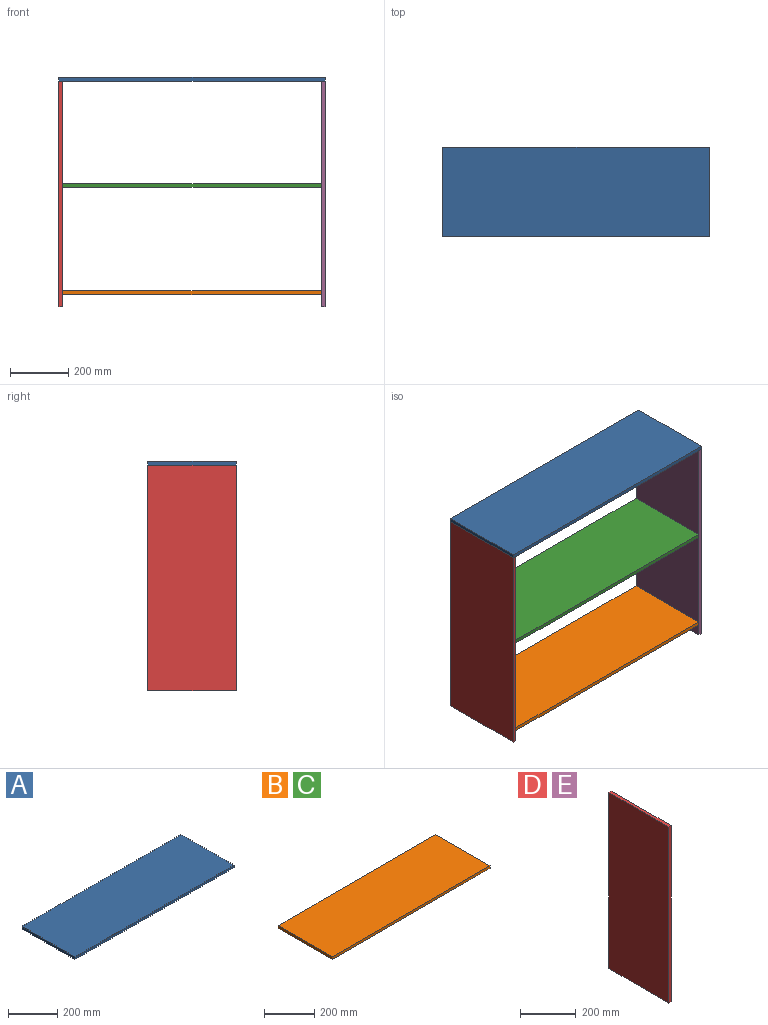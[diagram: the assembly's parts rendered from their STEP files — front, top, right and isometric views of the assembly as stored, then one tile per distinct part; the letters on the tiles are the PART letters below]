
ASSEMBLY  parts=5 mates=10
PART A: 6 faces, bbox 914.4x304.8x12.7 mm
  f0: plane 304.8x12.7mm, normal (-1,0,0), area 3871mm2, adj f1,f3,f4,f5
  f1: plane 914.4x304.8mm, normal (0,0,-1), area 278709.1mm2, adj f0,f2,f4,f5
  f2: plane 304.8x12.7mm, normal (1,0,0), area 3871mm2, adj f1,f3,f4,f5
  f3: plane 914.4x304.8mm, normal (0,0,1), area 278709.1mm2, adj f0,f2,f4,f5
  f4: plane 914.4x12.7mm, normal (0,-1,0), area 11612.9mm2, adj f0,f1,f2,f3
  f5: plane 914.4x12.7mm, normal (0,1,0), area 11612.9mm2, adj f0,f1,f2,f3
PART B: 6 faces, bbox 889x304.8x12.7 mm
  f0: plane 304.8x12.7mm, normal (-1,0,0), area 3871mm2, adj f1,f3,f4,f5
  f1: plane 889x304.8mm, normal (0,0,-1), area 270967.2mm2, adj f0,f2,f4,f5
  f2: plane 304.8x12.7mm, normal (1,0,0), area 3871mm2, adj f1,f3,f4,f5
  f3: plane 889x304.8mm, normal (0,0,1), area 270967.2mm2, adj f0,f2,f4,f5
  f4: plane 889x12.7mm, normal (0,-1,0), area 11290.3mm2, adj f0,f1,f2,f3
  f5: plane 889x12.7mm, normal (0,1,0), area 11290.3mm2, adj f0,f1,f2,f3
PART C: same geometry as B
PART D: 6 faces, bbox 12.7x304.8x774.7 mm
  f0: plane 774.7x304.8mm, normal (-1,0,0), area 236128.6mm2, adj f1,f3,f4,f5
  f1: plane 304.8x12.7mm, normal (0,0,-1), area 3871mm2, adj f0,f2,f4,f5
  f2: plane 774.7x304.8mm, normal (1,0,0), area 236128.6mm2, adj f1,f3,f4,f5
  f3: plane 304.8x12.7mm, normal (0,0,1), area 3871mm2, adj f0,f2,f4,f5
  f4: plane 774.7x12.7mm, normal (0,-1,0), area 9838.7mm2, adj f0,f1,f2,f3
  f5: plane 774.7x12.7mm, normal (0,1,0), area 9838.7mm2, adj f0,f1,f2,f3
PART E: same geometry as D
PLACE A t=(-237.16,185.54,636.95)mm
PLACE B t=(-224.46,185.54,-96.47)mm
PLACE C rot(axis=(0,0,1),0deg) t=(-224.46,185.54,271.83)mm
PLACE D t=(-237.16,185.54,-137.75)mm fixed
PLACE E t=(664.54,185.54,-137.75)mm
MATE planar D.f2 <-> C.f0  axis (1,0,0) through (-224.46,33.14,249.6)mm
MATE fastened E.f3 <-> A.f1  axis (0,0,1) through (670.89,33.14,636.95)mm
MATE planar D.f4 <-> C.f4  axis (0,-1,0) through (-230.81,-119.26,249.6)mm
MATE planar D.f0 <-> A.f0  axis (-1,0,0) through (-237.16,33.14,249.6)mm
MATE parallel D.f1 <-> B.f1  axis (0,0,-1) through (-230.81,33.14,-137.75)mm
MATE planar D.f2 <-> B.f0  axis (1,0,0) through (-224.46,33.14,249.6)mm
MATE planar A.f2 <-> E.f2  axis (1,0,0) through (677.24,33.14,643.3)mm
MATE parallel B.f3 <-> C.f3  axis (0,0,1) through (220.04,33.14,-83.77)mm
MATE fastened A.f1 <-> D.f3  axis (0,0,-1) through (220.04,33.14,636.95)mm
MATE planar D.f4 <-> B.f4  axis (0,-1,0) through (-230.81,-119.26,249.6)mm
